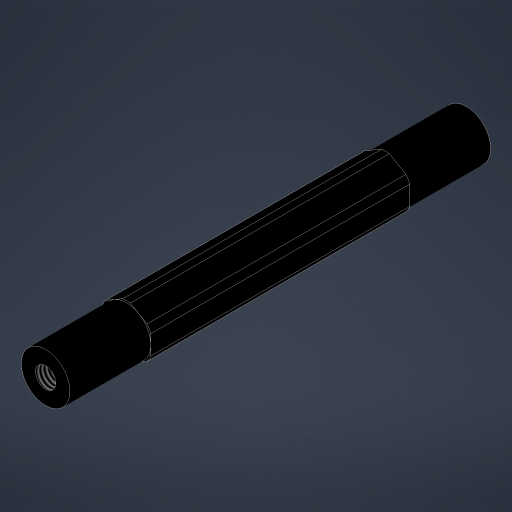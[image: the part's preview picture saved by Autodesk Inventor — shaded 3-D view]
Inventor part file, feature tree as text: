
AUTODESK INVENTOR PART (.ipt)
format: ipt  version: 2023.4 (Build 274418000, 418)  size: 254,976 bytes
history: native  units: in
note: dims shown in document units (in); Inventor stores cm internally (conversion verified against a paired STEP export)
features: extrude x3, projected_geometry x3, hole x1, mirror x1, sketch x1
ambient origin geometry x8: Origin, YZ Plane, XZ Plane, XY Plane, X Axis, Y Axis, Z Axis, Center Point
bodies: Solid1 (feature_tree)
feature tree (9):
  extrude  "Extrusion1"  Depth=0.375in
  hole  "Hole1"  [1 undecoded]
  extrude  "Extrusion3"  Depth=0.625in TaperAngle=0.0deg
  extrude  "Extrusion4"  Depth=0.375in
  mirror  "Mirror2"
  sketch  "Sketch5"  dims[d2=0.0in d9=0.38in d10=0.385in d11=0.25in d12=0.5635in d13=1.0in d14=0.8108in d16=0.7in d17=0.0in d18=0.0in d19=0.625in d20=0.0in d21=0.375in d22=0.5in d23=0.0344in d24=0.5in d25=0.0344in]
  projected_geometry  "Projected Loop2"
  projected_geometry  "Project Cut Edges1"
  projected_geometry  "Project Cut Edges2"
note: 1 required parameter value undecoded (feature->parameter linkage not recoverable at this tier; creation-order binding heuristic only, values carry confidence <= 0.55)
